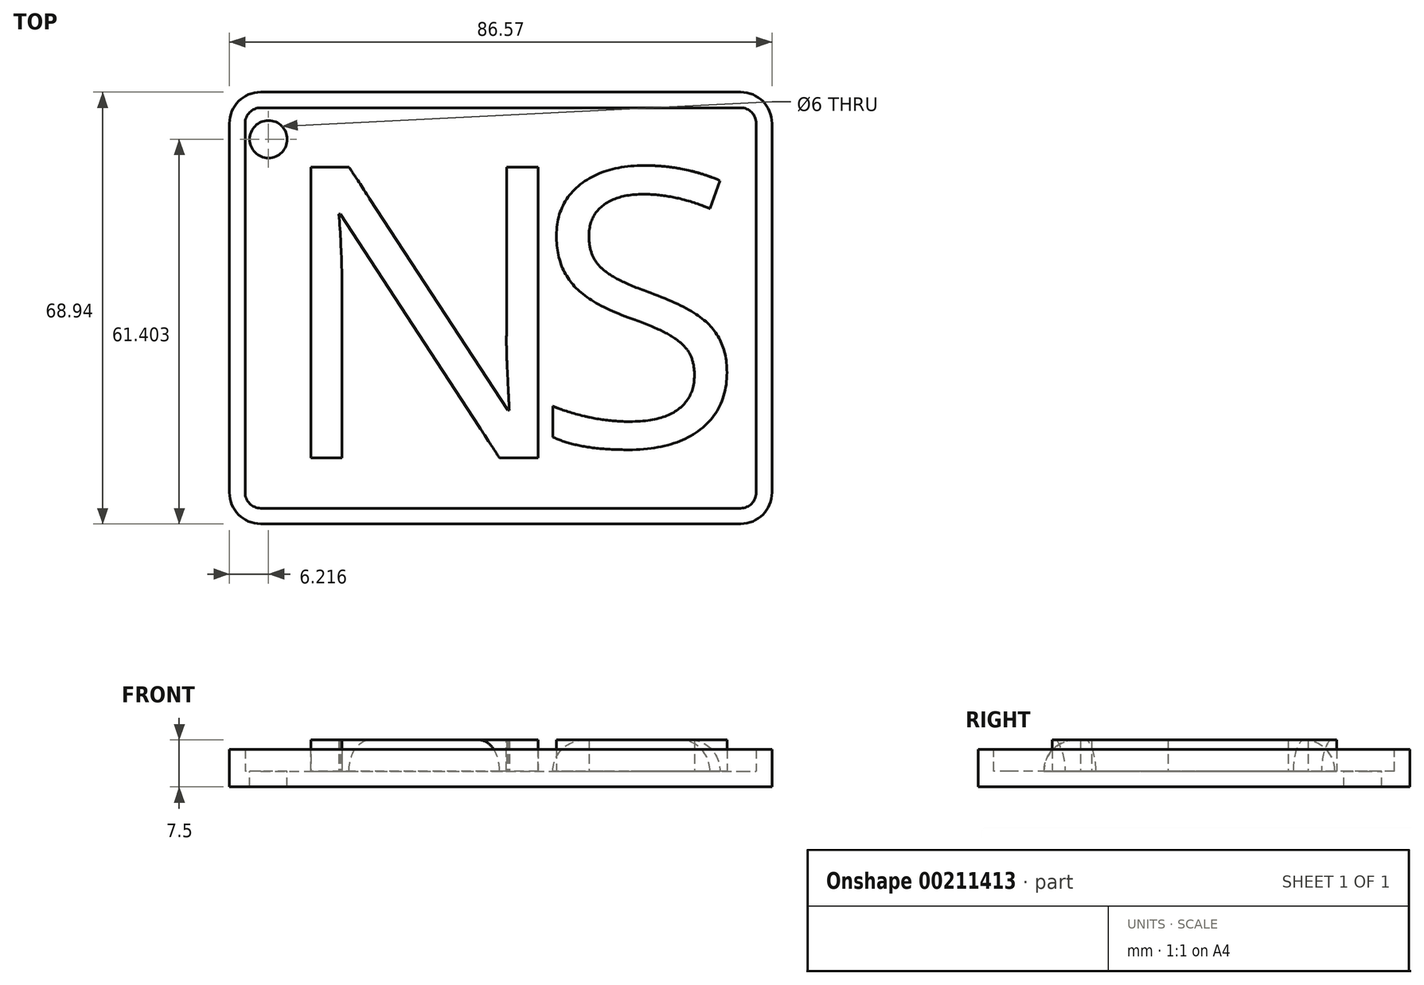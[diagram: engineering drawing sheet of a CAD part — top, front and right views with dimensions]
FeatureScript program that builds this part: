
annotation { "Feature Type Name" : "Feature", "Feature Type Description" : "" }
export const myFeature = defineFeature(function(context is Context, id is Id, definition is map)
    precondition{}
    {
        {
            var Q0;
            Q0=qCreatedBy(makeId("Top.planeOp"),FACE);
            var sketch = newSketch(context, id + "F0", { "sketchPlane" : qUnion([Q0])});
            skLineSegment(sketch, "E0.bottom", {"start": v(-39.76, 50.43) * mm, "end": v(46.81, 50.43) * mm});
            skLineSegment(sketch, "E0.top", {"start": v(-39.76, -18.5) * mm, "end": v(46.81, -18.5) * mm});
            skLineSegment(sketch, "E0.left", {"start": v(-39.76, 50.43) * mm, "end": v(-39.76, -18.5) * mm});
            skLineSegment(sketch, "E0.right", {"start": v(46.81, 50.43) * mm, "end": v(46.81, -18.5) * mm});
            skSolve(sketch);
        }
        {
            var Q0;
            Q0 = qSketchRegion(id + "F0", true);
            extrude(context, id + "F1", {"entities" : qUnion([Q0]), "depth" : 6 * mm});
        }
        {
            var Q0;
            Q0=makeQuery(id+"F1.opExtrude","CAP_FACE",FACE,{"disambiguationData":[OSD([sQuery(id+"F0.wireOp",EDGE,"E0.bottom"),sQuery(id+"F0.wireOp",EDGE,"E0.top"),sQuery(id+"F0.wireOp",EDGE,"E0.left"),sQuery(id+"F0.wireOp",EDGE,"E0.right")])],"isStart":false});
            var sketch = newSketch(context, id + "F2", { "sketchPlane" : qUnion([Q0])});
            skLineSegment(sketch, "E1.bottom", {"start": v(-36.44, 46.17) * mm, "end": v(42.6, 46.17) * mm});
            skLineSegment(sketch, "E1.top", {"start": v(-36.44, -13.98) * mm, "end": v(42.6, -13.98) * mm});
            skLineSegment(sketch, "E1.left", {"start": v(-36.44, 46.17) * mm, "end": v(-36.44, -13.98) * mm});
            skLineSegment(sketch, "E1.right", {"start": v(42.6, 46.17) * mm, "end": v(42.6, -13.98) * mm});
            skSolve(sketch);
        }
        {
            var Q0;
            Q0=makeQuery(id+"F2.imprint","IMPRINT",FACE,{"disambiguationData":[TD([[makeQuery(id+"F2.imprint","IMPRINT",EDGE,{"derivedFrom":sQuery(id+"F2.wireOp",EDGE,"E1.bottom")}),-1.0]])]});
            extrude(context, id + "F3", {"entities" : qUnion([Q0]), "operationType" : NewBodyOperationType.ADD, "oppositeDirection" : true, "depth" : 6 * mm});
        }
        {
            var Q0;
            Q0=makeQuery(id+"F1.opExtrude","SWEPT_EDGE",EDGE,{"disambiguationData":[OSD([sQuery(id+"F0.wireOp",EDGE,"E0.top"),sQuery(id+"F0.wireOp",EDGE,"E0.left")])]});
            var Q1;
            Q1=makeQuery(id+"F1.opExtrude","SWEPT_EDGE",EDGE,{"disambiguationData":[OSD([sQuery(id+"F0.wireOp",EDGE,"E0.top"),sQuery(id+"F0.wireOp",EDGE,"E0.right")])]});
            var Q2;
            Q2=makeQuery(id+"F1.opExtrude","SWEPT_EDGE",EDGE,{"disambiguationData":[OSD([sQuery(id+"F0.wireOp",EDGE,"E0.bottom"),sQuery(id+"F0.wireOp",EDGE,"E0.left")])]});
            var Q3;
            Q3=makeQuery(id+"F1.opExtrude","SWEPT_EDGE",EDGE,{"disambiguationData":[OSD([sQuery(id+"F0.wireOp",EDGE,"E0.bottom"),sQuery(id+"F0.wireOp",EDGE,"E0.right")])]});
            fillet(context, id + "F4", {"entities" : qUnion([Q0, Q1, Q2, Q3]), "radius" : 5 * mm, "tangentPropagation" : true, "allowEdgeOverflow" : false});
        }
        {
            var Q0;
            Q0=makeQuery(id+"F1.opExtrude","CAP_FACE",FACE,{"disambiguationData":[OSD([sQuery(id+"F0.wireOp",EDGE,"E0.bottom"),sQuery(id+"F0.wireOp",EDGE,"E0.top"),sQuery(id+"F0.wireOp",EDGE,"E0.left"),sQuery(id+"F0.wireOp",EDGE,"E0.right")])],"isStart":false});
            shell(context, id + "F5", {"entities" : qUnion([Q0]), "thickness" : 2.5 * mm});
        }
        {
            var Q0;
            Q0=makeQuery(id+"F5.opShell","OFFSET_FACE",FACE,{"disambiguationData":[OSD([sQuery(id+"F0.wireOp",EDGE,"E0.bottom"),sQuery(id+"F0.wireOp",EDGE,"E0.top"),sQuery(id+"F0.wireOp",EDGE,"E0.left"),sQuery(id+"F0.wireOp",EDGE,"E0.right")])]});
            var sketch = newSketch(context, id + "F6", { "sketchPlane" : qUnion([Q0])});
            skText(sketch, "E2", { "text": "NS", "fontName": "OpenSans-Regular.ttf"});
            const initialGuessF6  = {"E2": [-0.03798, -0.00607, 1, 0, 0.04453]};
            skSetInitialGuess(sketch, initialGuessF6);
            skSolve(sketch);
        }
        {
            var Q0;
            Q0=makeQuery(id+"F6.imprint","IMPRINT",FACE,{"disambiguationData":[TD([[makeQuery(id+"F6.imprint","IMPRINT",EDGE,{"derivedFrom":sQuery(id+"F6.wireOp",EDGE,"E2.sketch_text.stroke-15")}),-1.0]])]});
            extrude(context, id + "F7", {"entities" : qUnion([Q0]), "operationType" : NewBodyOperationType.ADD, "depth" : 5 * mm});
        }
        {
            var Q0;
            Q0=makeQuery(id+"F5.opShell","OFFSET_FACE",FACE,{"disambiguationData":[OSD([sQuery(id+"F0.wireOp",EDGE,"E0.bottom"),sQuery(id+"F0.wireOp",EDGE,"E0.top"),sQuery(id+"F0.wireOp",EDGE,"E0.left"),sQuery(id+"F0.wireOp",EDGE,"E0.right")])]});
            var sketch = newSketch(context, id + "F8", { "sketchPlane" : qUnion([Q0])});
            skText(sketch, "E3", { "text": "N", "fontName": "OpenSans-Regular.ttf"});
            const initialGuessF8  = {"E3": [-0.03316, -0.008, 1, 0, 0.04685]};
            skSetInitialGuess(sketch, initialGuessF8);
            skSolve(sketch);
        }
        {
            var Q0;
            Q0=makeQuery(id+"F8.imprint","IMPRINT",FACE,{"disambiguationData":[TD([[makeQuery(id+"F8.imprint","IMPRINT",EDGE,{"derivedFrom":sQuery(id+"F8.wireOp",EDGE,"E3.sketch_text.stroke-0")}),-1.0]])]});
            extrude(context, id + "F9", {"entities" : qUnion([Q0]), "operationType" : NewBodyOperationType.ADD, "depth" : 5 * mm});
        }
        {
            var Q0;
            Q0=makeQuery(id+"F5.opShell","OFFSET_FACE",FACE,{"disambiguationData":[OSD([sQuery(id+"F0.wireOp",EDGE,"E0.bottom"),sQuery(id+"F0.wireOp",EDGE,"E0.top"),sQuery(id+"F0.wireOp",EDGE,"E0.left"),sQuery(id+"F0.wireOp",EDGE,"E0.right")])]});
            var sketch = newSketch(context, id + "F10", { "sketchPlane" : qUnion([Q0])});
            skPoint(sketch, "E4", {"position": v(-33.54, 42.9) * mm});
            skSolve(sketch);
        }
        {
            var Q0;
            Q0=sQuery(id+"F10.wireOp",VERTEX,"E4");
            var Q1;
            Q1=makeQuery(id+"F1.opExtrude","SWEPT_BODY",BODY,{"disambiguationData":[OSD([sQuery(id+"F0.wireOp",EDGE,"E0.bottom"),sQuery(id+"F0.wireOp",EDGE,"E0.top"),sQuery(id+"F0.wireOp",EDGE,"E0.left"),sQuery(id+"F0.wireOp",EDGE,"E0.right")])]});
            hole(context, id + "F11", {"style" : HoleStyle.SIMPLE, "endStyle" : HoleEndStyle.THROUGH, "holeDiameter" : 6 * mm, "locations" : qUnion([Q0]), "scope" : qUnion([Q1]), "isTappedThrough" : true});
        }
        {
            var Q0;
            Q0=makeQuery(id+"F7.opExtrude","CAP_EDGE",EDGE,{"disambiguationData":[OSD([sQuery(id+"F6.wireOp",EDGE,"E2.sketch_text.stroke-18")])],"isStart":false});
            fillet(context, id + "F12", {"entities" : qUnion([Q0]), "radius" : 5 * mm, "tangentPropagation" : true, "allowEdgeOverflow" : false});
        }
        {
            var Q0;
            Q0=makeQuery(id+"F7.opExtrude","CAP_EDGE",EDGE,{"disambiguationData":[OSD([sQuery(id+"F6.wireOp",EDGE,"E2.sketch_text.stroke-31")])],"isStart":false});
            fillet(context, id + "F13", {"entities" : qUnion([Q0]), "radius" : 5 * mm, "tangentPropagation" : true, "allowEdgeOverflow" : false});
        }
        {
            var Q0;
            Q0=makeQuery(id+"F9.opExtrude","CAP_EDGE",EDGE,{"disambiguationData":[OSD([sQuery(id+"F8.wireOp",EDGE,"E3.sketch_text.stroke-0")])],"isStart":false});
            var Q1;
            Q1=makeQuery(id+"F9.opExtrude","CAP_EDGE",EDGE,{"disambiguationData":[OSD([sQuery(id+"F8.wireOp",EDGE,"E3.sketch_text.stroke-5")])],"isStart":false});
            var Q2;
            Q2=makeQuery(id+"F9.opExtrude","CAP_EDGE",EDGE,{"disambiguationData":[OSD([sQuery(id+"F8.wireOp",EDGE,"E3.sketch_text.stroke-13")])],"isStart":false});
            var Q3;
            Q3=makeQuery(id+"F9.opExtrude","CAP_EDGE",EDGE,{"disambiguationData":[OSD([sQuery(id+"F8.wireOp",EDGE,"E3.sketch_text.stroke-7")])],"isStart":false});
            fillet(context, id + "F14", {"entities" : qUnion([Q0, Q1, Q2, Q3]), "radius" : 5 * mm, "tangentPropagation" : true, "allowEdgeOverflow" : false});
        }
    });
